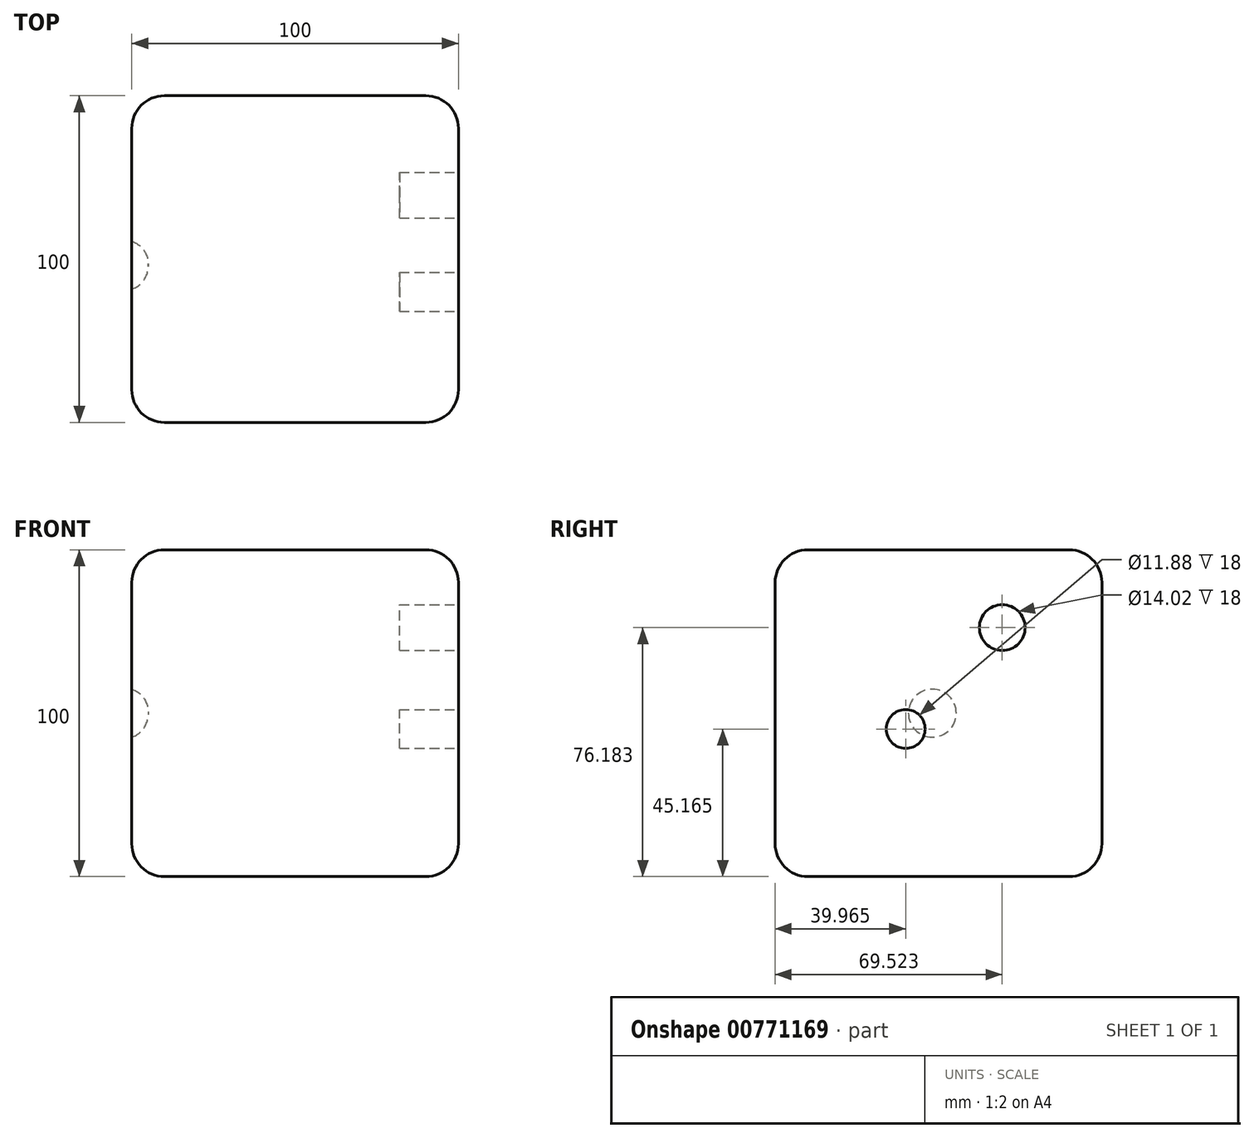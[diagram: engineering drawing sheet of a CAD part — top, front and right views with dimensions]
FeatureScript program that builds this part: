
annotation { "Feature Type Name" : "Feature", "Feature Type Description" : "" }
export const myFeature = defineFeature(function(context is Context, id is Id, definition is map)
    precondition{}
    {
        {
            var Q0;
            Q0=qCreatedBy(makeId("Top.planeOp"),FACE);
            var sketch = newSketch(context, id + "F0", { "sketchPlane" : qUnion([Q0])});
            skLineSegment(sketch, "E0.bottom", {"start": v(50, -50) * mm, "end": v(-50, -50) * mm});
            skLineSegment(sketch, "E0.top", {"start": v(50, 50) * mm, "end": v(-50, 50) * mm});
            skLineSegment(sketch, "E0.left", {"start": v(50, -50) * mm, "end": v(50, 50) * mm});
            skLineSegment(sketch, "E0.right", {"start": v(-50, -50) * mm, "end": v(-50, 50) * mm});
            skPoint(sketch, "E0.middle", {"position": v(0, 0) * mm});
            skSolve(sketch);
        }
        {
            var Q0;
            Q0 = qSketchRegion(id + "F0", true);
            extrude(context, id + "F1", {"entities" : qUnion([Q0]), "depth" : 100 * mm, "offsetDistance" : 25 * mm});
        }
        {
            var Q0;
            Q0=makeQuery(id+"F1.opExtrude","SWEPT_EDGE",EDGE,{"disambiguationData":[OSD([sQuery(id+"F0.wireOp",EDGE,"E0.bottom"),sQuery(id+"F0.wireOp",EDGE,"E0.right")])]});
            var Q1;
            Q1=makeQuery(id+"F1.opExtrude","CAP_EDGE",EDGE,{"disambiguationData":[OSD([sQuery(id+"F0.wireOp",EDGE,"E0.bottom")])],"isStart":true});
            var Q2;
            Q2=makeQuery(id+"F1.opExtrude","SWEPT_EDGE",EDGE,{"disambiguationData":[OSD([sQuery(id+"F0.wireOp",EDGE,"E0.bottom"),sQuery(id+"F0.wireOp",EDGE,"E0.left")])]});
            var Q3;
            Q3=makeQuery(id+"F1.opExtrude","CAP_EDGE",EDGE,{"disambiguationData":[OSD([sQuery(id+"F0.wireOp",EDGE,"E0.right")])],"isStart":false});
            var Q4;
            Q4=makeQuery(id+"F1.opExtrude","CAP_EDGE",EDGE,{"disambiguationData":[OSD([sQuery(id+"F0.wireOp",EDGE,"E0.top")])],"isStart":false});
            var Q5;
            Q5=makeQuery(id+"F1.opExtrude","CAP_EDGE",EDGE,{"disambiguationData":[OSD([sQuery(id+"F0.wireOp",EDGE,"E0.left")])],"isStart":false});
            var Q6;
            Q6=makeQuery(id+"F1.opExtrude","CAP_EDGE",EDGE,{"disambiguationData":[OSD([sQuery(id+"F0.wireOp",EDGE,"E0.bottom")])],"isStart":false});
            var Q7;
            Q7=makeQuery(id+"F1.opExtrude","CAP_EDGE",EDGE,{"disambiguationData":[OSD([sQuery(id+"F0.wireOp",EDGE,"E0.right")])],"isStart":true});
            var Q8;
            Q8=makeQuery(id+"F1.opExtrude","SWEPT_EDGE",EDGE,{"disambiguationData":[OSD([sQuery(id+"F0.wireOp",EDGE,"E0.top"),sQuery(id+"F0.wireOp",EDGE,"E0.right")])]});
            var Q9;
            Q9=makeQuery(id+"F1.opExtrude","CAP_EDGE",EDGE,{"disambiguationData":[OSD([sQuery(id+"F0.wireOp",EDGE,"E0.top")])],"isStart":true});
            var Q10;
            Q10=makeQuery(id+"F1.opExtrude","SWEPT_EDGE",EDGE,{"disambiguationData":[OSD([sQuery(id+"F0.wireOp",EDGE,"E0.top"),sQuery(id+"F0.wireOp",EDGE,"E0.left")])]});
            var Q11;
            Q11=makeQuery(id+"F1.opExtrude","CAP_EDGE",EDGE,{"disambiguationData":[OSD([sQuery(id+"F0.wireOp",EDGE,"E0.left")])],"isStart":true});
            fillet(context, id + "F2", {"entities" : qUnion([Q0, Q1, Q2, Q3, Q4, Q5, Q6, Q7, Q8, Q9, Q10, Q11]), "radius" : 10 * mm, "tangentPropagation" : true, "allowEdgeOverflow" : false});
        }
        {
            var Q0;
            Q0=makeQuery(id+"F1.opExtrude","SWEPT_FACE",FACE,{"disambiguationData":[OSD([sQuery(id+"F0.wireOp",EDGE,"E0.right")])]});
            var sketch = newSketch(context, id + "F3", { "sketchPlane" : qUnion([Q0])});
            skLineSegment(sketch, "E1", {"start": v(0, 90) * mm, "end": v(3.75, 10) * mm, "construction": true});
            skLineSegment(sketch, "E2", {"start": v(-40, 50) * mm, "end": v(40, 50) * mm, "construction": true});
            skCircle(sketch, "E3", {"center": v(1.88, 50) * mm, "radius": 7.33 * mm});
            skSolve(sketch);
        }
        {
            var Q0;
            Q0 = qSketchRegion(id + "F3", true);
            extrude(context, id + "F4", {"entities" : qUnion([Q0]), "operationType" : NewBodyOperationType.REMOVE, "oppositeDirection" : true, "depth" : 5 * mm, "offsetDistance" : 25 * mm});
        }
        {
            var Q0;
            Q0=makeQuery(id+"F1.opExtrude","SWEPT_FACE",FACE,{"disambiguationData":[OSD([sQuery(id+"F0.wireOp",EDGE,"E0.left")])]});
            var sketch = newSketch(context, id + "F5", { "sketchPlane" : qUnion([Q0])});
            skCircle(sketch, "E4", {"center": v(19.52, 76.18) * mm, "radius": 7 * mm});
            skCircle(sketch, "E5", {"center": v(-10.04, 45.16) * mm, "radius": 5.94 * mm});
            skSolve(sketch);
        }
        {
            var Q0;
            Q0=makeQuery(id+"F5.imprint","IMPRINT",FACE,{"disambiguationData":[TD([[makeQuery(id+"F5.imprint","IMPRINT",EDGE,{"derivedFrom":sQuery(id+"F5.wireOp",EDGE,"E4")}),1.0]])]});
            var Q1;
            Q1=makeQuery(id+"F5.imprint","IMPRINT",FACE,{"disambiguationData":[TD([[makeQuery(id+"F5.imprint","IMPRINT",EDGE,{"derivedFrom":sQuery(id+"F5.wireOp",EDGE,"E5")}),1.0]])]});
            var Q2;
            Q2=sQuery(id+"F5.wireOp",EDGE,"E4");
            extrude(context, id + "F6", {"entities" : qUnion([Q0, Q1]), "operationType" : NewBodyOperationType.REMOVE, "surfaceEntities" : qUnion([Q2]), "oppositeDirection" : true, "depth" : 18 * mm, "offsetDistance" : 25 * mm});
        }
        {
            var Q0;
            {var subQ0=sQuery(id+"F0.wireOp",EDGE,"E0.left");var subQ1=sQuery(id+"F0.wireOp",EDGE,"E0.bottom");Q0=makeQuery(id+"F2.opFillet","BLEND_FACE",FACE,{"disambiguationData":[OSD([subQ1,subQ0]),TDD([makeQuery(id+"F1.opExtrude","CAP_VERTEX",VERTEX,{"disambiguationData":[OSD([subQ1,subQ0])],"isStart":true})])]});}
            var Q1;
            Q1=makeQuery(id+"F4.boolean.opBoolean","COPY",EDGE,{"derivedFrom":makeQuery(id+"F4.opExtrude","CAP_EDGE",EDGE,{"disambiguationData":[OSD([sQuery(id+"F3.wireOp",EDGE,"E3")])],"isStart":false})});
            fillet(context, id + "F7", {"entities" : qUnion([Q0, Q1]), "radius" : 7.24 * mm, "tangentPropagation" : true, "allowEdgeOverflow" : false});
        }
    });
